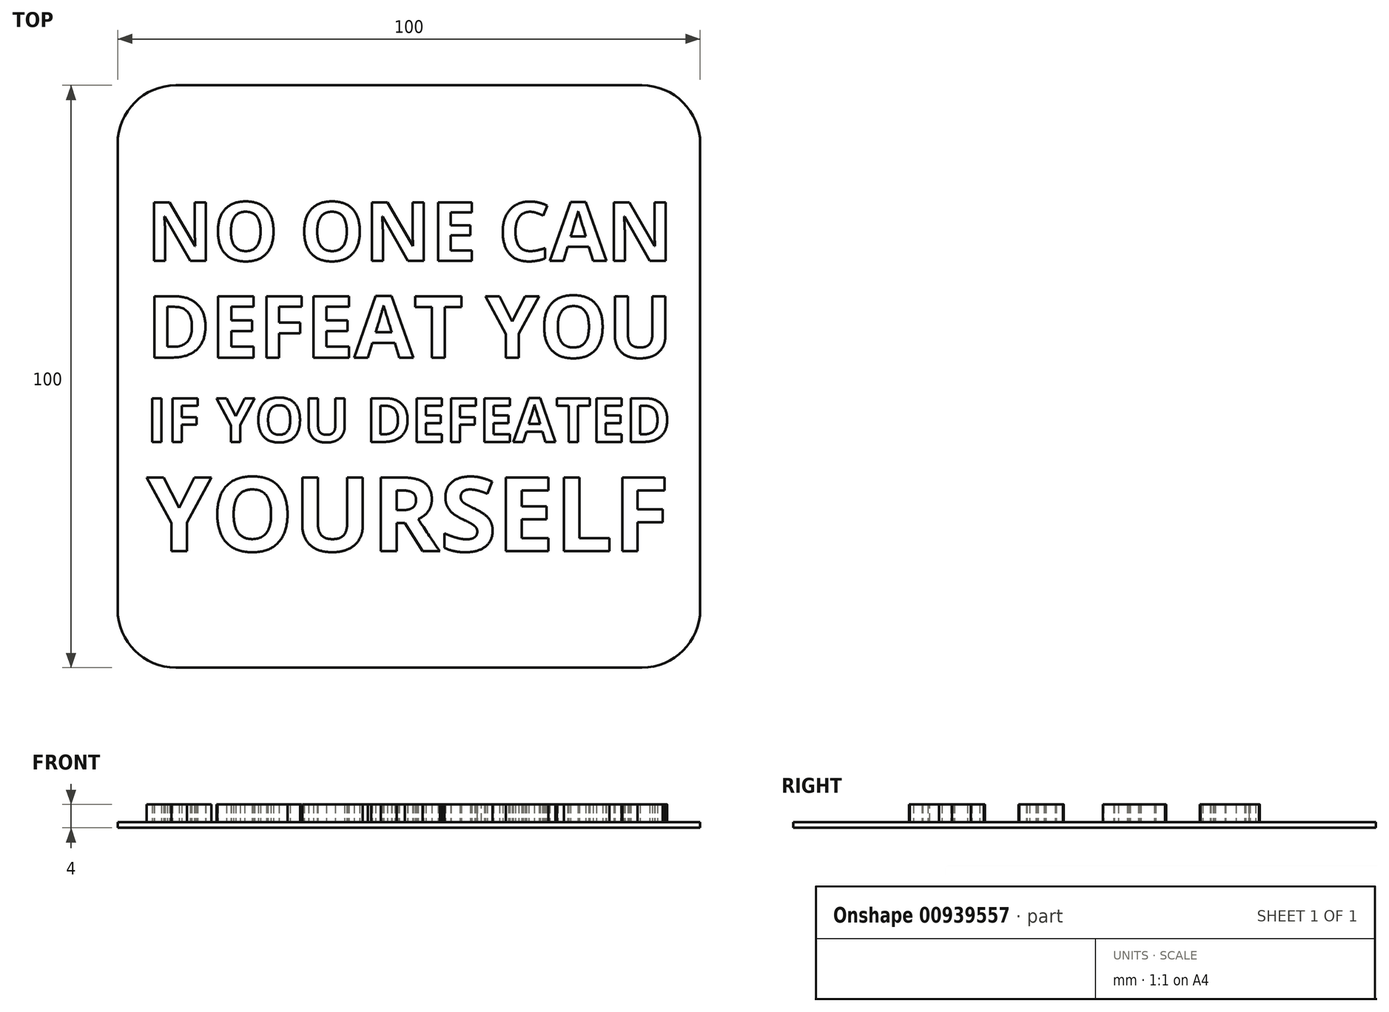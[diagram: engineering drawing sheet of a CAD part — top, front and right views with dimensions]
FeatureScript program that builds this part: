
annotation { "Feature Type Name" : "Feature", "Feature Type Description" : "" }
export const myFeature = defineFeature(function(context is Context, id is Id, definition is map)
    precondition{}
    {
        {
            var Q0;
            Q0=qCreatedBy(makeId("Top.planeOp"),FACE);
            var sketch = newSketch(context, id + "F0", { "sketchPlane" : qUnion([Q0])});
            skLineSegment(sketch, "E0.bottom", {"start": v(50, -50) * mm, "end": v(-50, -50) * mm});
            skLineSegment(sketch, "E0.top", {"start": v(50, 50) * mm, "end": v(-50, 50) * mm});
            skLineSegment(sketch, "E0.left", {"start": v(50, -50) * mm, "end": v(50, 50) * mm});
            skLineSegment(sketch, "E0.right", {"start": v(-50, -50) * mm, "end": v(-50, 50) * mm});
            skPoint(sketch, "E0.middle", {"position": v(0, 0) * mm});
            skSolve(sketch);
        }
        {
            var Q0;
            Q0 = qSketchRegion(id + "F0", true);
            extrude(context, id + "F1", {"entities" : qUnion([Q0]), "depth" : 1 * mm, "offsetDistance" : 25 * mm});
        }
        {
            var Q0;
            Q0=makeQuery(id+"F1.opExtrude","CAP_FACE",FACE,{"disambiguationData":[OSD([sQuery(id+"F0.wireOp",EDGE,"E0.bottom"),sQuery(id+"F0.wireOp",EDGE,"E0.top"),sQuery(id+"F0.wireOp",EDGE,"E0.left"),sQuery(id+"F0.wireOp",EDGE,"E0.right")])],"isStart":false});
            var sketch = newSketch(context, id + "F2", { "sketchPlane" : qUnion([Q0])});
            skText(sketch, "E1", { "text": "NO ONE CAN ", "fontName": "OpenSans-Bold.ttf"});
            skText(sketch, "E2", { "text": "DEFEAT YOU", "fontName": "OpenSans-Bold.ttf"});
            skText(sketch, "E3", { "text": "IF YOU DEFEATED", "fontName": "OpenSans-Bold.ttf"});
            skText(sketch, "E4", { "text": "YOURSELF", "fontName": "OpenSans-Bold.ttf"});
            const initialGuessF2  = {"E1": [-0.045, 0.0199, 1, 0, 0.0101], "E2": [-0.045, 0.00326, 1, 0, 0.01063], "E3": [-0.045, -0.01123, 1, 0, 0.00757], "E4": [-0.045, -0.03, 1, 0, 0.01277]};
            skSetInitialGuess(sketch, initialGuessF2);
            skSolve(sketch);
        }
        {
            var Q0;
            Q0 = qSketchRegion(id + "F2", true);
            extrude(context, id + "F3", {"entities" : qUnion([Q0]), "operationType" : NewBodyOperationType.ADD, "depth" : 3 * mm, "offsetDistance" : 25 * mm});
        }
        {
            var Q0;
            Q0=makeQuery(id+"F1.opExtrude","SWEPT_EDGE",EDGE,{"disambiguationData":[OSD([sQuery(id+"F0.wireOp",EDGE,"E0.top"),sQuery(id+"F0.wireOp",EDGE,"E0.right")])]});
            var Q1;
            Q1=makeQuery(id+"F1.opExtrude","SWEPT_EDGE",EDGE,{"disambiguationData":[OSD([sQuery(id+"F0.wireOp",EDGE,"E0.top"),sQuery(id+"F0.wireOp",EDGE,"E0.left")])]});
            var Q2;
            Q2=makeQuery(id+"F1.opExtrude","SWEPT_EDGE",EDGE,{"disambiguationData":[OSD([sQuery(id+"F0.wireOp",EDGE,"E0.bottom"),sQuery(id+"F0.wireOp",EDGE,"E0.right")])]});
            var Q3;
            Q3=makeQuery(id+"F1.opExtrude","SWEPT_EDGE",EDGE,{"disambiguationData":[OSD([sQuery(id+"F0.wireOp",EDGE,"E0.bottom"),sQuery(id+"F0.wireOp",EDGE,"E0.left")])]});
            fillet(context, id + "F4", {"entities" : qUnion([Q0, Q1, Q2, Q3]), "radius" : 10 * mm, "tangentPropagation" : true, "allowEdgeOverflow" : false});
        }
    });
